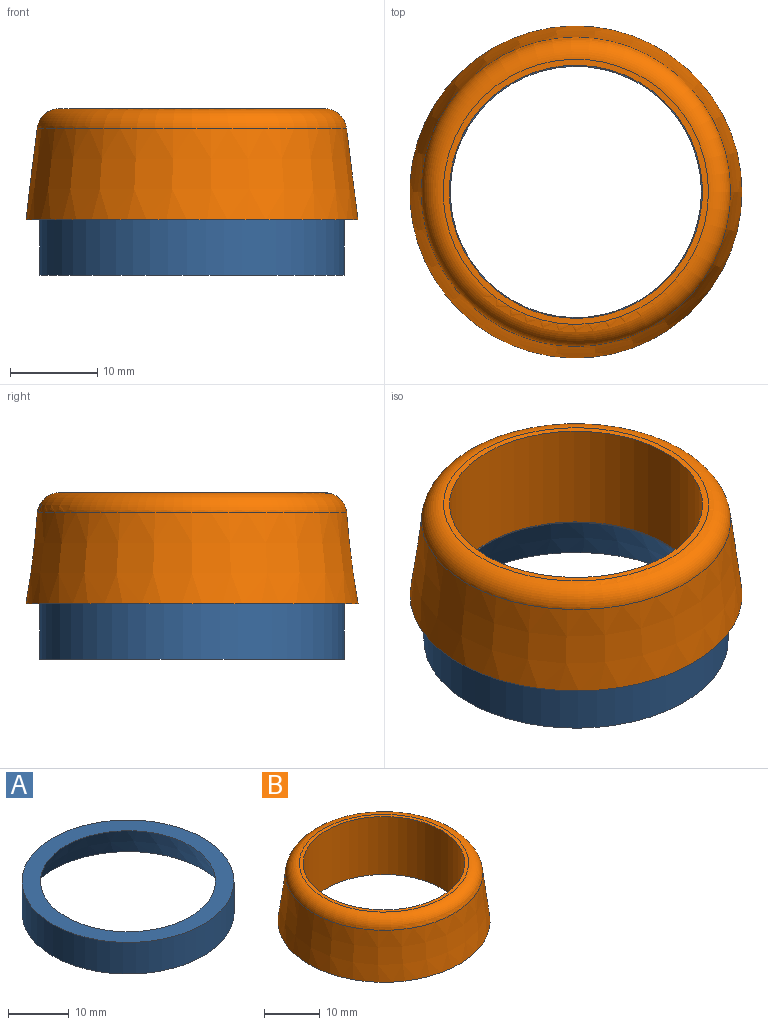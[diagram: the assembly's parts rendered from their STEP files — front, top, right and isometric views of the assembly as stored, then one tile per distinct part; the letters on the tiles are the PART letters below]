
ASSEMBLY  parts=2 mates=1
PART A: 3 faces, bbox 34.8x34.8x6.4 mm
  f0: cylinder r=17.41mm len=34.82mm, axis (0,0,-1), area 694.7mm2, adj f1,f2
  f1: cone r=14.36mm half-angle=25.6deg, axis (0,0,-1), area 703.1mm2, adj f0,f2
  f2: plane 34.82x34.82mm, normal (0,0,1), area 304.3mm2, adj f0,f1
PART B: 5 faces, bbox 38.3x38.3x12.7 mm
  f0: plane 38x38mm, normal (0,0,-1), area 475.5mm2, adj f1,f3
  f1: cone r=17.41mm half-angle=7.1deg, axis (0,0,-1), area 1216.8mm2, adj f0,f4
  f2: plane 30.34x30.34mm, normal (0,0,1), area 64.4mm2, adj f3,f4
  f3: cylinder r=14.48mm len=28.96mm, axis (0,0,1), area 1155.3mm2, adj f0,f2
  f4: torus R=15.17mm, axis (0,0,-1), area 385.7mm2, adj f1,f2
PLACE A rot(axis=(0,0,1),180deg) t=(20.68,-29.4,-1.81)mm
PLACE B rot(axis=(0,0,1),180deg) t=(3.27,-29.4,4.54)mm
MATE fastened B.f1 <-> A.f0  axis (0,0,-1) through (3.27,-29.4,4.54)mm
